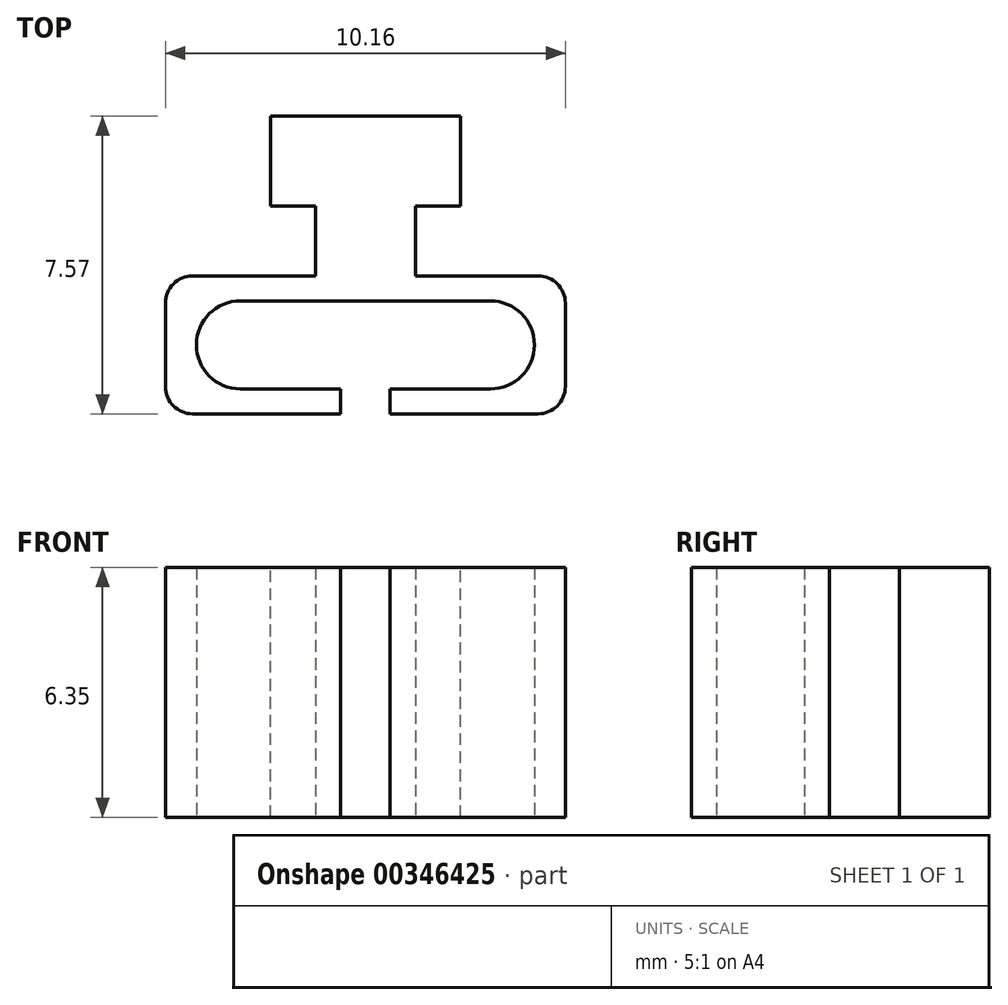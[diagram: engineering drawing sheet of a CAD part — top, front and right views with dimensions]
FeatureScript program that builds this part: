
annotation { "Feature Type Name" : "Feature", "Feature Type Description" : "" }
export const myFeature = defineFeature(function(context is Context, id is Id, definition is map)
    precondition{}
    {
        {
            var Q0;
            Q0=qCreatedBy(makeId("Top.planeOp"),FACE);
            var sketch = newSketch(context, id + "F0", { "sketchPlane" : qUnion([Q0])});
            skLineSegment(sketch, "E0.bottom", {"start": v(-91.04, 1.78) * mm, "end": v(-88.5, 1.78) * mm});
            skLineSegment(sketch, "E0.top", {"start": v(-91.04, 0) * mm, "end": v(-88.5, 0) * mm});
            skLineSegment(sketch, "E0.left", {"start": v(-91.04, 1.78) * mm, "end": v(-91.04, 0) * mm});
            skLineSegment(sketch, "E0.right", {"start": v(-88.5, 1.78) * mm, "end": v(-88.5, 0) * mm});
            skSolve(sketch);
        }
        {
            var Q0;
            Q0 = qSketchRegion(id + "F0", true);
            extrude(context, id + "F1", {"entities" : qUnion([Q0]), "depth" : 25.4 * mm});
        }
        {
            var Q0;
            Q0=makeQuery(id+"F1.opExtrude","SWEPT_FACE",FACE,{"disambiguationData":[OSD([sQuery(id+"F0.wireOp",EDGE,"E0.bottom")])]});
            var sketch = newSketch(context, id + "F2", { "sketchPlane" : qUnion([Q0])});
            skLineSegment(sketch, "E1.bottom", {"start": v(87.36, 0) * mm, "end": v(92.19, 0) * mm});
            skLineSegment(sketch, "E1.top", {"start": v(87.36, 25.4) * mm, "end": v(92.19, 25.4) * mm});
            skLineSegment(sketch, "E1.left", {"start": v(87.36, 0) * mm, "end": v(87.36, 25.4) * mm});
            skLineSegment(sketch, "E1.right", {"start": v(92.19, 0) * mm, "end": v(92.19, 25.4) * mm});
            skPoint(sketch, "E1.middle", {"position": v(89.77, 12.7) * mm});
            skPoint(sketch, "E1.middle.positionSnap0", {"position": v(89.77, 0) * mm});
            skPoint(sketch, "E1.middle.positionSnap1", {"position": v(91.04, 12.7) * mm});
            skPoint(sketch, "E1.centerSnap0", {"position": v(89.77, 0) * mm});
            skPoint(sketch, "E1.centerSnap1", {"position": v(91.04, 12.7) * mm});
            skSolve(sketch);
        }
        {
            var Q0;
            Q0 = qSketchRegion(id + "F2", true);
            extrude(context, id + "F3", {"entities" : qUnion([Q0]), "operationType" : NewBodyOperationType.ADD, "depth" : 2.3 * mm});
        }
        {
            var Q0;
            Q0=makeQuery(id+"F1.opExtrude","SWEPT_FACE",FACE,{"disambiguationData":[OSD([sQuery(id+"F0.wireOp",EDGE,"E0.top")])]});
            var sketch = newSketch(context, id + "F4", { "sketchPlane" : qUnion([Q0])});
            skSolve(sketch);
        }
        {
            var Q0;
            {var subQ0=sQuery(id+"F0.wireOp",EDGE,"E0.top");Q0=makeQuery(id+"F4.imprint","IMPRINT",FACE,{"disambiguationData":[TD([[makeQuery(id+"F4.imprint","IMPRINT",EDGE,{"derivedFrom":makeQuery(id+"F1.opExtrude","CAP_EDGE",EDGE,{"disambiguationData":[OSD([subQ0])],"isStart":true})}),1.0]])]});}
            var sketch = newSketch(context, id + "F5", { "sketchPlane" : qUnion([Q0])});
            skLineSegment(sketch, "E2.0.0", {"start": v(-91.04, 25.4) * mm, "end": v(-91.04, 0) * mm});
            skLineSegment(sketch, "E2.0.1", {"start": v(-91.04, 0) * mm, "end": v(-88.5, 0) * mm});
            skLineSegment(sketch, "E2.0.2", {"start": v(-88.5, 0) * mm, "end": v(-88.5, 25.4) * mm});
            skLineSegment(sketch, "E2.0.3", {"start": v(-88.5, 25.4) * mm, "end": v(-91.04, 25.4) * mm});
            skLineSegment(sketch, "E3.bottom", {"start": v(-84.7, 0) * mm, "end": v(-94.85, 0) * mm});
            skLineSegment(sketch, "E3.top", {"start": v(-84.7, 25.4) * mm, "end": v(-94.85, 25.4) * mm});
            skLineSegment(sketch, "E3.left", {"start": v(-84.7, 0) * mm, "end": v(-84.7, 25.4) * mm});
            skLineSegment(sketch, "E3.right", {"start": v(-94.85, 0) * mm, "end": v(-94.85, 25.4) * mm});
            skPoint(sketch, "E3.middle", {"position": v(-89.77, 12.7) * mm});
            skPoint(sketch, "E3.middle.positionSnap0", {"position": v(-88.5, 12.7) * mm});
            skPoint(sketch, "E3.middle.positionSnap1", {"position": v(-89.77, 0) * mm});
            skPoint(sketch, "E3.centerSnap0", {"position": v(-88.5, 12.7) * mm});
            skPoint(sketch, "E3.centerSnap1", {"position": v(-89.77, 0) * mm});
            skSolve(sketch);
        }
        {
            var Q0;
            Q0 = qSketchRegion(id + "F5", true);
            extrude(context, id + "F6", {"entities" : qUnion([Q0]), "operationType" : NewBodyOperationType.ADD, "depth" : 3.5 * mm});
        }
        {
            var Q0;
            Q0=makeQuery(id+"F6.boolean.opBoolean","MERGE",FACE,{"derivedFrom":[makeQuery(id+"F3.boolean.opBoolean","MERGE",FACE,{"derivedFrom":[makeQuery(id+"F1.opExtrude","CAP_FACE",FACE,{"disambiguationData":[OSD([sQuery(id+"F0.wireOp",EDGE,"E0.bottom"),sQuery(id+"F0.wireOp",EDGE,"E0.top"),sQuery(id+"F0.wireOp",EDGE,"E0.left"),sQuery(id+"F0.wireOp",EDGE,"E0.right")])],"isStart":true}),makeQuery(id+"F3.opExtrude","SWEPT_FACE",FACE,{"disambiguationData":[OSD([sQuery(id+"F2.wireOp",EDGE,"E1.bottom")])]})]}),makeQuery(id+"F6.opExtrude","SWEPT_FACE",FACE,{"disambiguationData":[OSD([sQuery(id+"F5.wireOp",EDGE,"E3.bottom")])]})]});
            var sketch = newSketch(context, id + "F7", { "sketchPlane" : qUnion([Q0])});
            skCircle(sketch, "E4", {"center": v(-86.6, 1.75) * mm, "radius": 1.12 * mm});
            skPoint(sketch, "E4.centerSnap0", {"position": v(-84.7, 1.75) * mm});
            skPoint(sketch, "E4.centerSnap1", {"position": v(-86.6, 0) * mm});
            skCircle(sketch, "E5", {"center": v(-92.95, 1.75) * mm, "radius": 1.12 * mm});
            skPoint(sketch, "E5.centerSnap0", {"position": v(-94.85, 1.75) * mm});
            skPoint(sketch, "E5.centerSnap1", {"position": v(-92.95, 0) * mm});
            skLineSegment(sketch, "E6", {"start": v(-86.6, 0.64) * mm, "end": v(-92.95, 0.64) * mm});
            skLineSegment(sketch, "E7", {"start": v(-86.6, 2.87) * mm, "end": v(-89.15, 2.87) * mm});
            skLineSegment(sketch, "E8", {"start": v(-92.95, 2.87) * mm, "end": v(-90.4, 2.87) * mm});
            skLineSegment(sketch, "E9", {"start": v(-89.15, 2.87) * mm, "end": v(-89.15, 3.5) * mm});
            skLineSegment(sketch, "E10", {"start": v(-90.4, 2.87) * mm, "end": v(-90.4, 3.5) * mm});
            skSolve(sketch);
        }
        {
            var Q0;
            Q0 = qSketchRegion(id + "F7", true);
            var Q1;
            {var subQ0=sQuery(id+"F7.wireOp",EDGE,"E6");Q1=makeQuery(id+"F7.imprint","IMPRINT",FACE,{"disambiguationData":[TD([[makeQuery(id+"F7.imprint","IMPRINT",EDGE,{"derivedFrom":subQ0}),-1.0]])]});}
            extrude(context, id + "F8", {"entities" : qUnion([Q0, Q1]), "operationType" : NewBodyOperationType.REMOVE, "oppositeDirection" : true, "depth" : 25.4 * mm});
        }
        {
            var Q0;
            Q0=makeQuery(id+"F6.opExtrude","CAP_EDGE",EDGE,{"disambiguationData":[OSD([sQuery(id+"F5.wireOp",EDGE,"E3.right")])],"isStart":true});
            var Q1;
            Q1=makeQuery(id+"F6.opExtrude","CAP_EDGE",EDGE,{"disambiguationData":[OSD([sQuery(id+"F5.wireOp",EDGE,"E3.right")])],"isStart":false});
            var Q2;
            Q2=makeQuery(id+"F6.opExtrude","CAP_EDGE",EDGE,{"disambiguationData":[OSD([sQuery(id+"F5.wireOp",EDGE,"E3.left")])],"isStart":false});
            var Q3;
            Q3=makeQuery(id+"F6.opExtrude","CAP_EDGE",EDGE,{"disambiguationData":[OSD([sQuery(id+"F5.wireOp",EDGE,"E3.left")])],"isStart":true});
            fillet(context, id + "F9", {"entities" : qUnion([Q0, Q1, Q2, Q3]), "radius" : ((.5 + .88) / 2) * mm, "tangentPropagation" : true, "allowEdgeOverflow" : false});
        }
        {
            var Q0;
            Q0=makeQuery(id+"F6.boolean.opBoolean","MERGE",FACE,{"derivedFrom":[makeQuery(id+"F3.boolean.opBoolean","MERGE",FACE,{"derivedFrom":[makeQuery(id+"F1.opExtrude","CAP_FACE",FACE,{"disambiguationData":[OSD([sQuery(id+"F0.wireOp",EDGE,"E0.bottom"),sQuery(id+"F0.wireOp",EDGE,"E0.top"),sQuery(id+"F0.wireOp",EDGE,"E0.left"),sQuery(id+"F0.wireOp",EDGE,"E0.right")])],"isStart":true}),makeQuery(id+"F3.opExtrude","SWEPT_FACE",FACE,{"disambiguationData":[OSD([sQuery(id+"F2.wireOp",EDGE,"E1.bottom")])]})]}),makeQuery(id+"F6.opExtrude","SWEPT_FACE",FACE,{"disambiguationData":[OSD([sQuery(id+"F5.wireOp",EDGE,"E3.bottom")])]})]});
            extrude(context, id + "F10", {"entities" : qUnion([Q0]), "operationType" : NewBodyOperationType.REMOVE, "oppositeDirection" : true, "depth" : 19.05 * mm});
        }
    });
